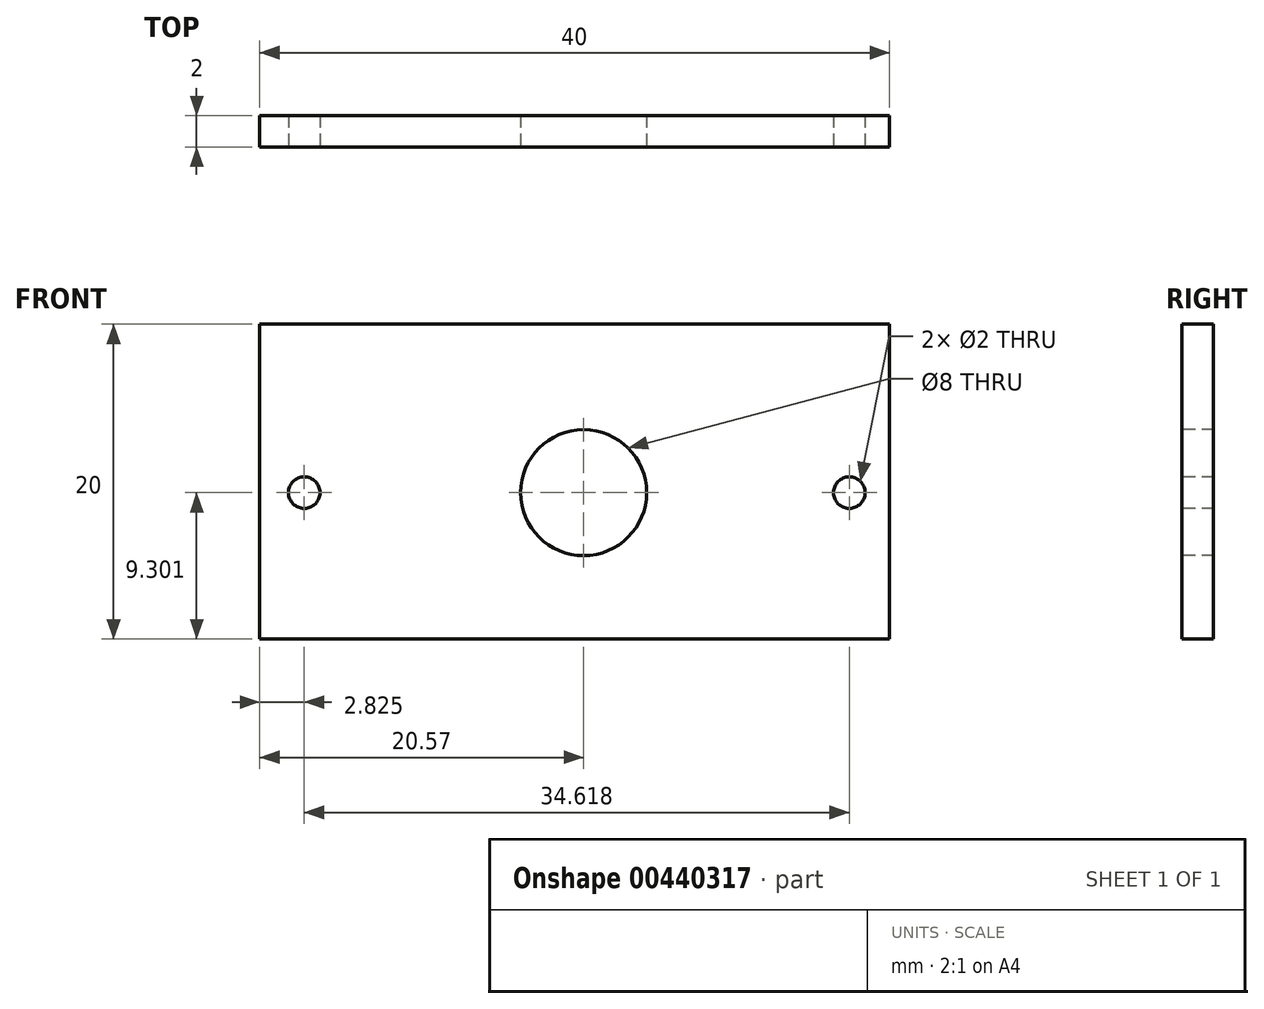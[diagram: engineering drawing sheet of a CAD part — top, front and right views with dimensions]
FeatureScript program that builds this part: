
annotation { "Feature Type Name" : "Feature", "Feature Type Description" : "" }
export const myFeature = defineFeature(function(context is Context, id is Id, definition is map)
    precondition{}
    {
        {
            var Q0;
            Q0=qCreatedBy(makeId("Top.planeOp"),FACE);
            var sketch = newSketch(context, id + "F0", { "sketchPlane" : qUnion([Q0])});
            skLineSegment(sketch, "E0", {"start": v(-58.55, 15.04) * mm, "end": v(-18.55, 15.04) * mm});
            skLineSegment(sketch, "E1", {"start": v(-58.55, 15.04) * mm, "end": v(-58.55, 17.04) * mm});
            skLineSegment(sketch, "E2", {"start": v(-18.55, 15.04) * mm, "end": v(-18.55, 17.04) * mm});
            skLineSegment(sketch, "E3", {"start": v(-18.55, 17.04) * mm, "end": v(-58.55, 17.04) * mm});
            skSolve(sketch);
        }
        {
            var Q0;
            Q0=makeQuery(id+"F0.imprint","IMPRINT",FACE,{"disambiguationData":[TD([[makeQuery(id+"F0.imprint","IMPRINT",EDGE,{"derivedFrom":sQuery(id+"F0.wireOp",EDGE,"E0")}),1.0]])]});
            extrude(context, id + "F1", {"entities" : qUnion([Q0]), "depth" : 20 * mm});
        }
        {
            var Q0;
            Q0=qCreatedBy(makeId("Front.planeOp"),FACE);
            cPlane(context, id + "F2", {"entities" : qUnion([Q0]), "cplaneType" : CPlaneType.OFFSET, "offset" : 0 * mm, "width" : 150 * mm, "height" : 150 * mm});
        }
        {
            var Q0;
            Q0=qCreatedBy(id+"F2.planeOp",FACE);
            var sketch = newSketch(context, id + "F3", { "sketchPlane" : qUnion([Q0])});
            skPoint(sketch, "E4", {"position": v(-37.98, 9.3) * mm});
            skPoint(sketch, "E5", {"position": v(-55.72, 9.3) * mm});
            skPoint(sketch, "E6", {"position": v(-21.1, 9.3) * mm});
            skSolve(sketch);
        }
        {
            var Q0;
            Q0=sQuery(id+"F3.wireOp",VERTEX,"E4");
            var Q1;
            Q1=makeQuery(id+"F1.opExtrude","SWEPT_BODY",BODY,{"disambiguationData":[OSD([sQuery(id+"F0.wireOp",EDGE,"E0"),sQuery(id+"F0.wireOp",EDGE,"E1"),sQuery(id+"F0.wireOp",EDGE,"E2"),sQuery(id+"F0.wireOp",EDGE,"E3")])]});
            hole(context, id + "F4", {"style" : HoleStyle.SIMPLE, "endStyle" : HoleEndStyle.THROUGH, "holeDiameter" : 8 * mm, "isTappedThrough" : true, "tappedDepth" : 12 * mm, "tapClearance" : 3, "locations" : qUnion([Q0]), "scope" : qUnion([Q1])});
        }
        {
            var Q0;
            Q0=sQuery(id+"F3.wireOp",VERTEX,"E5");
            var Q1;
            Q1=sQuery(id+"F3.wireOp",VERTEX,"E6");
            var Q2;
            Q2=makeQuery(id+"F1.opExtrude","SWEPT_BODY",BODY,{"disambiguationData":[OSD([sQuery(id+"F0.wireOp",EDGE,"E0"),sQuery(id+"F0.wireOp",EDGE,"E1"),sQuery(id+"F0.wireOp",EDGE,"E2"),sQuery(id+"F0.wireOp",EDGE,"E3")])]});
            hole(context, id + "F5", {"style" : HoleStyle.SIMPLE, "endStyle" : HoleEndStyle.THROUGH, "holeDiameter" : 2 * mm, "isTappedThrough" : true, "tappedDepth" : 12 * mm, "tapClearance" : 3, "locations" : qUnion([Q0, Q1]), "scope" : qUnion([Q2])});
        }
    });
